# Revit family: Practibox_S_cofrecito_saliente_12_módulos_réf_135101_a_135214
name_source: partatom
category: Equipement électrique
revit_build: Autodesk Revit 2018 (Build: 20170223_1515(x64)
units: mm (PartAtom-declared; Revit-internal decimal feet)

## family parameters
Basée sur le plan de construction = Non
Configuration du panneau = Deux colonnes, circuits au sein
Cote de connecteur circulaire = Utiliser le diamètre
Couper avec des vides une fois chargée = Non
Numéro OmniClass = 23.80.30.11.17
Partagée = Non
Point de calcul de pièce = Non
Titre OmniClass = Distribution Boards and Control Panels
Toujours verticalement = Oui
Type d'élément = Tableau de raccordement

## types (16) — shared parameters
Condiciones Generales de Uso = https://export.legrand.com
Fabricant = "Legrand"
"Legrand"
"Legrand"
URL = www.legrand.com
anchura = 328 mm  [stored 1.07612 ft]
profundidad = 210 mm  [stored 0.688976 ft]

## per-type parameters (varying)
| type | 1R | 2R | 3R | 4R | Altura | Bornas N | Bornas T | Ina | puerta B 1 r | puerta B 2 r | puerta B 3 r | puerta B 4 r | puerta T 1 r | puerta T 2 r | puerta T 3 r | puerta T 4 r | puerta blanca | puerta transparencia | tamaño |
| Practibox_S_cofrecito_saliente_12_módulos_135201 | Oui | Non | Non | Non | 236 mm | 24 salidas Icc 6kA | 24 salidas Icc 6kA | 63A | Oui | Non | Non | Non | Non | Non | Non | Non | Oui | Non | 1 fila |
| Practibox_S_cofrecito_saliente_24_módulos_135102 | Non | Oui | Non | Non | 386 mm  [stored 1.2664 ft] |  |  | 90A | Non | Oui | Non | Non | Non | Non | Non | Non | Oui | Non | 2 rangées |
| Practibox_S_cofrecito_saliente_36_módulos_135103 | Non | Non | Oui | Non | 536 mm |  |  | 90A | Non | Non | Oui | Non | Non | Non | Non | Non | Oui | Non | 3 fila |
| Practibox_S_cofrecito_saliente_48_módulos_135104 | Non | Non | Non | Oui | 766 mm  [stored 2.51312 ft] |  |  | 90A | Non | Non | Non | Oui | Non | Non | Non | Non | Oui | Non | 4 fila |
| Practibox_S_cofrecito_saliente_12_módulos_135211 | Oui | Non | Non | Non | 236 mm | 24 salidas Icc 6kA | 24 salidas Icc 6kA | 63A | Non | Non | Non | Non | Oui | Non | Non | Non | Non | Oui | 1 fila |
| Practibox_S_cofrecito_saliente_12_módulos_135101 | Oui | Non | Non | Non | 236 mm |  |  | 63A | Oui | Non | Non | Non | Non | Non | Non | Non | Oui | Non | 1 fila |
| Practibox_S_cofrecito_saliente_12_módulos_135111 | Oui | Non | Non | Non | 236 mm |  |  | 63A | Non | Non | Non | Non | Oui | Non | Non | Non | Non | Oui | 1 fila |
| Practibox_S_cofrecito_saliente_24_módulos_135112 | Non | Oui | Non | Non | 386 mm  [stored 1.2664 ft] |  |  | 90A | Non | Non | Non | Non | Non | Oui | Non | Non | Non | Oui | 2 fila |
| Practibox_S_cofrecito_saliente_24_módulos_135212 | Non | Oui | Non | Non | 386 mm  [stored 1.2664 ft] | 24 salidas Icc 6kA | 24 salidas Icc 6kA | 90A | Non | Non | Non | Non | Non | Oui | Non | Non | Non | Oui | 2 fila |
| Practibox_S_cofrecito_saliente_24_módulos_135202 | Non | Oui | Non | Non | 386 mm  [stored 1.2664 ft] | 24 salidas Icc 6kA | 24 salidas Icc 6kA | 90A | Non | Oui | Non | Non | Non | Non | Non | Non | Oui | Non | 2 fila |
| Practibox_S_cofrecito_saliente_36_módulos_135113 | Non | Non | Oui | Non | 536 mm |  |  | 90A | Non | Non | Non | Non | Non | Non | Oui | Non | Non | Oui | 3 fila |
| Practibox_S_cofrecito_saliente_36_módulos_135213 | Non | Non | Oui | Non | 536 mm | 24 salidas Icc 6kA | 24 salidas Icc 6kA | 90A | Non | Non | Non | Non | Non | Non | Oui | Non | Non | Oui | 3 fila |
| Practibox_S_cofrecito_saliente_36_módulos_135203 | Non | Non | Oui | Non | 536 mm | 24 salidas Icc 6kA | 24 salidas Icc 6kA | 90A | Non | Non | Oui | Non | Non | Non | Non | Non | Oui | Non | 3 fila |
| Practibox_S_cofrecito_saliente_48_módulos_135114 | Non | Non | Non | Oui | 766 mm  [stored 2.51312 ft] |  |  | 90A | Non | Non | Non | Non | Non | Non | Non | Oui | Non | Oui | 4 fila |
| Practibox_S_cofrecito_saliente_48_módulos_135214 | Non | Non | Non | Oui | 766 mm  [stored 2.51312 ft] | 24 salidas Icc 6kA | 24 salidas Icc 6kA | 90A | Non | Non | Non | Non | Non | Non | Non | Oui | Non | Oui | 4 fila |
| Practibox_S_cofrecito_saliente_48_módulos_135204 | Non | Non | Non | Oui | 766 mm  [stored 2.51312 ft] | 24 salidas Icc 6kA | 24 salidas Icc 6kA | 90A | Non | Non | Non | Oui | Non | Non | Non | Non | Oui | Non | 4 fila |

note: column(s) folded — value = type name in every type: Description

note: [stored X ft] marks values corroborated as IEEE doubles in the binary element streams (Revit-internal decimal feet)
